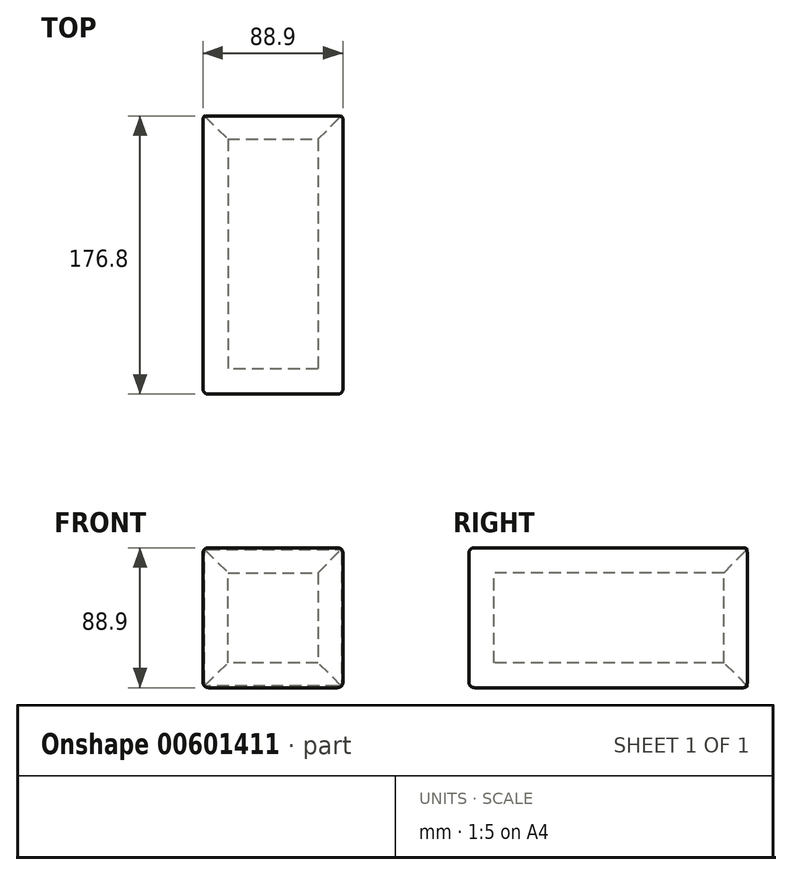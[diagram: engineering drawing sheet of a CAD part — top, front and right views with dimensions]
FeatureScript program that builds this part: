
annotation { "Feature Type Name" : "Feature", "Feature Type Description" : "" }
export const myFeature = defineFeature(function(context is Context, id is Id, definition is map)
    precondition{}
    {
        {
            var Q0;
            Q0=qCreatedBy(makeId("Front.planeOp"),FACE);
            var sketch = newSketch(context, id + "F0", { "sketchPlane" : qUnion([Q0])});
            skLineSegment(sketch, "E0.bottom", {"start": v(-44.45, 44.45) * mm, "end": v(44.45, 44.45) * mm});
            skLineSegment(sketch, "E0.top", {"start": v(-44.45, -44.45) * mm, "end": v(44.45, -44.45) * mm});
            skLineSegment(sketch, "E0.left", {"start": v(-44.45, 44.45) * mm, "end": v(-44.45, -44.45) * mm});
            skLineSegment(sketch, "E0.right", {"start": v(44.45, 44.45) * mm, "end": v(44.45, -44.45) * mm});
            skPoint(sketch, "E0.middle", {"position": v(0, 0) * mm});
            skLineSegment(sketch, "E1.bottom", {"start": v(-28.57, 28.58) * mm, "end": v(28.58, 28.58) * mm});
            skLineSegment(sketch, "E1.top", {"start": v(-28.58, -28.58) * mm, "end": v(28.57, -28.58) * mm});
            skLineSegment(sketch, "E1.left", {"start": v(-28.57, 28.58) * mm, "end": v(-28.58, -28.58) * mm});
            skLineSegment(sketch, "E1.right", {"start": v(28.58, 28.58) * mm, "end": v(28.57, -28.58) * mm});
            skSolve(sketch);
        }
        {
            var Q0;
            Q0=makeQuery(id+"F0.imprint","IMPRINT",FACE,{"disambiguationData":[TD([[makeQuery(id+"F0.imprint","IMPRINT",EDGE,{"derivedFrom":sQuery(id+"F0.wireOp",EDGE,"E0.bottom")}),-1.0]])]});
            extrude(context, id + "F1", {"entities" : qUnion([Q0]), "oppositeDirection" : true, "depth" : 177.8 * mm, "offsetDistance" : 25.4 * mm});
        }
        {
            var Q0;
            Q0=makeQuery(id+"F0.imprint","IMPRINT",FACE,{"disambiguationData":[TD([[makeQuery(id+"F0.imprint","IMPRINT",EDGE,{"derivedFrom":sQuery(id+"F0.wireOp",EDGE,"E0.bottom")}),-1.0]])]});
            var Q1;
            Q1=makeQuery(id+"F0.imprint","IMPRINT",FACE,{"disambiguationData":[TD([[makeQuery(id+"F0.imprint","IMPRINT",EDGE,{"derivedFrom":sQuery(id+"F0.wireOp",EDGE,"E1.bottom")}),-1.0]])]});
            extrude(context, id + "F2", {"entities" : qUnion([Q0, Q1]), "operationType" : NewBodyOperationType.ADD, "oppositeDirection" : true, "depth" : 15.88 * mm, "offsetDistance" : 25.4 * mm});
        }
        {
            var Q0;
            Q0=makeQuery(id+"F1.opExtrude","SWEPT_EDGE",EDGE,{"disambiguationData":[OSD([sQuery(id+"F0.wireOp",EDGE,"E0.bottom"),sQuery(id+"F0.wireOp",EDGE,"E0.right")])]});
            var Q1;
            Q1=makeQuery(id+"F1.opExtrude","CAP_EDGE",EDGE,{"disambiguationData":[OSD([sQuery(id+"F0.wireOp",EDGE,"E0.bottom")])],"isStart":true});
            var Q2;
            Q2=makeQuery(id+"F1.opExtrude","CAP_EDGE",EDGE,{"disambiguationData":[OSD([sQuery(id+"F0.wireOp",EDGE,"E0.right")])],"isStart":true});
            var Q3;
            Q3=makeQuery(id+"F1.opExtrude","CAP_EDGE",EDGE,{"disambiguationData":[OSD([sQuery(id+"F0.wireOp",EDGE,"E0.top")])],"isStart":true});
            var Q4;
            Q4=makeQuery(id+"F1.opExtrude","SWEPT_EDGE",EDGE,{"disambiguationData":[OSD([sQuery(id+"F0.wireOp",EDGE,"E0.top"),sQuery(id+"F0.wireOp",EDGE,"E0.right")])]});
            var Q5;
            Q5=makeQuery(id+"F1.opExtrude","CAP_EDGE",EDGE,{"disambiguationData":[OSD([sQuery(id+"F0.wireOp",EDGE,"E0.left")])],"isStart":true});
            var Q6;
            Q6=makeQuery(id+"F1.opExtrude","SWEPT_EDGE",EDGE,{"disambiguationData":[OSD([sQuery(id+"F0.wireOp",EDGE,"E0.top"),sQuery(id+"F0.wireOp",EDGE,"E0.left")])]});
            var Q7;
            Q7=makeQuery(id+"F1.opExtrude","SWEPT_FACE",FACE,{"disambiguationData":[OSD([sQuery(id+"F0.wireOp",EDGE,"E0.bottom")])]});
            var Q8;
            Q8=makeQuery(id+"F1.opExtrude","CAP_EDGE",EDGE,{"disambiguationData":[OSD([sQuery(id+"F0.wireOp",EDGE,"E0.left")])],"isStart":false});
            var Q9;
            Q9=makeQuery(id+"F1.opExtrude","CAP_EDGE",EDGE,{"disambiguationData":[OSD([sQuery(id+"F0.wireOp",EDGE,"E0.top")])],"isStart":false});
            var Q10;
            Q10=makeQuery(id+"F1.opExtrude","CAP_EDGE",EDGE,{"disambiguationData":[OSD([sQuery(id+"F0.wireOp",EDGE,"E0.right")])],"isStart":false});
            fillet(context, id + "F3", {"entities" : qUnion([Q0, Q1, Q2, Q3, Q4, Q5, Q6, Q7, Q8, Q9, Q10]), "radius" : 3.43 * mm, "tangentPropagation" : true, "allowEdgeOverflow" : false});
        }
        {
            var Q0;
            Q0=makeQuery(id+"F1.opExtrude","CAP_EDGE",EDGE,{"disambiguationData":[OSD([sQuery(id+"F0.wireOp",EDGE,"E1.left")])],"isStart":false});
            var Q1;
            Q1=makeQuery(id+"F1.opExtrude","CAP_EDGE",EDGE,{"disambiguationData":[OSD([sQuery(id+"F0.wireOp",EDGE,"E1.top")])],"isStart":false});
            var Q2;
            Q2=makeQuery(id+"F1.opExtrude","CAP_EDGE",EDGE,{"disambiguationData":[OSD([sQuery(id+"F0.wireOp",EDGE,"E1.bottom")])],"isStart":false});
            var Q3;
            Q3=makeQuery(id+"F1.opExtrude","CAP_EDGE",EDGE,{"disambiguationData":[OSD([sQuery(id+"F0.wireOp",EDGE,"E1.right")])],"isStart":false});
            chamfer(context, id + "F4", {"entities" : qUnion([Q0, Q1, Q2, Q3]), "width" : 15.88 * mm, "tangentPropagation" : true});
        }
    });
